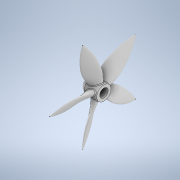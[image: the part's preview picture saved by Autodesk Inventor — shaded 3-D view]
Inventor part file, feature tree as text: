
AUTODESK INVENTOR PART (.ipt)
format: ipt  version: 2022 (Build 260153000, 153)  size: 1,681,408 bytes
history: native  units: mm
features: sketch x8, plane x4, fillet x2, loft x1, pattern_circular x1, revolve x1, extrude x1
ambient origin geometry x8: Origin, YZ Plane, XZ Plane, XY Plane, X Axis, Y Axis, Z Axis, Center Point
bodies: Solid1 (feature_tree)
feature tree (18):
  sketch  "Sketch1"  dims[d0=7.5mm d1=13.0mm]
  plane  "Work Plane1"
  plane  "Work Plane2"
  plane  "Work Plane3"
  plane  "Work Plane4"
  sketch  "Sketch2"  dims[d2=7.0mm]
  sketch  "Sketch3"  dims[d4=1.5mm]
  sketch  "Sketch4"  dims[d5=7.0mm]
  sketch  "Sketch5"  dims[d6=10.0mm]
  sketch  "Sketch6"  dims[d7=4.5mm]
  sketch  "Sketch7"  dims[d8=6.0mm]
  loft  "Loft1"
  pattern_circular  "Circular Pattern1"  Count=5  [1 undecoded]
  revolve  "Revolution1"  [1 undecoded]
  extrude  "Extrusion1"  Depth=3.0mm
  fillet  "Fillet1"  Radius=7.5mm
  fillet  "Fillet2"  Radius=2.0mm
  sketch  "Sketch8"  dims[d9=3.0mm d10=7.5mm d11=50.0mm d12=15.0mm d13=30.0mm d14=6.0mm d15=3.0mm d16=7.5mm d17=2.0mm d18=7.0mm d19=1.6mm d20=0.2mm d21=0.5mm d22=3.0mm d23=6.0mm d24=0.0mm d25=90.0deg d26=0.0mm d27=90.0deg d28=0.0mm d29=90.0deg d30=0.0mm d31=90.0deg d32=0.0mm d33=90.0deg d34=50.0mm d35=360.0deg d37=90.0deg d38=9.0mm d39=10.0mm d40=0.0mm d41=0.8mm d42=0.8mm]
note: 2 required parameter values undecoded (feature->parameter linkage not recoverable at this tier; creation-order binding heuristic only, values carry confidence <= 0.55)